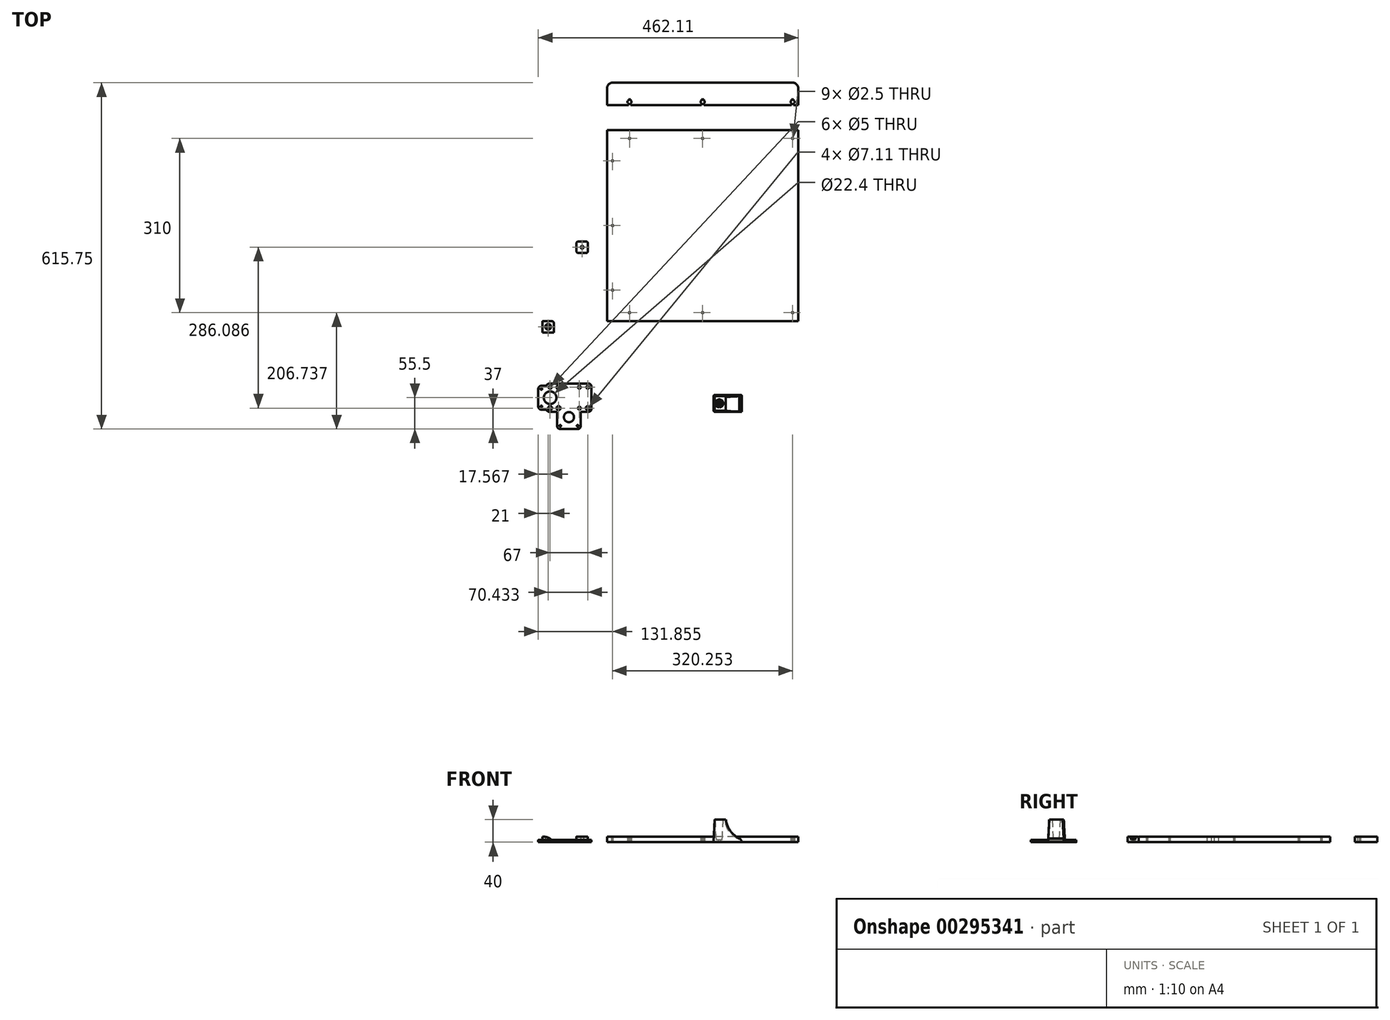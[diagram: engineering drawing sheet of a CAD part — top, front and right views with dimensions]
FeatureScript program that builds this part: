
annotation { "Feature Type Name" : "Feature", "Feature Type Description" : "" }
export const myFeature = defineFeature(function(context is Context, id is Id, definition is map)
    precondition{}
    {
        {
            var Q0;
            Q0=qCreatedBy(makeId("Top.planeOp"),FACE);
            var sketch = newSketch(context, id + "F0", { "sketchPlane" : qUnion([Q0])});
            skLineSegment(sketch, "E0.left", {"start": v(-18.5, 18.5) * mm, "end": v(-18.5, -18.5) * mm, "construction": true});
            skLineSegment(sketch, "E0.right", {"start": v(18.5, 18.5) * mm, "end": v(18.5, -18.5) * mm, "construction": true});
            skCircle(sketch, "E1", {"center": v(-18.5, 18.5) * mm, "radius": 3.56 * mm});
            skCircle(sketch, "E2", {"center": v(18.5, 18.5) * mm, "radius": 2.5 * mm});
            skCircle(sketch, "E3", {"center": v(18.5, -18.5) * mm, "radius": 2.5 * mm});
            skCircle(sketch, "E4", {"center": v(-18.5, -18.5) * mm, "radius": 3.56 * mm});
            skLineSegment(sketch, "E5.bottom", {"start": v(-35, 25) * mm, "end": v(35, 25) * mm});
            skLineSegment(sketch, "E5.top", {"start": v(-35, -25) * mm, "end": v(0.1, -25) * mm});
            skLineSegment(sketch, "E5.right", {"start": v(40, 20) * mm, "end": v(40, -20) * mm});
            skPoint(sketch, "E6.visualSharp", {"position": v(-40, 25) * mm});
            skArc(sketch, "E6.filletArc", {"start": v(-35, 25) * mm, "mid": v(-38.54, 23.54) * mm, "end": v(-40, 20) * mm});
            skPoint(sketch, "E7.visualSharp", {"position": v(40, 25) * mm});
            skArc(sketch, "E7.filletArc", {"start": v(40, 20) * mm, "mid": v(38.54, 23.54) * mm, "end": v(35, 25) * mm});
            skPoint(sketch, "E8.visualSharp", {"position": v(40, -25) * mm});
            skArc(sketch, "E8.filletArc", {"start": v(35, -25) * mm, "mid": v(38.54, -23.54) * mm, "end": v(40, -20) * mm});
            skPoint(sketch, "E9.visualSharp", {"position": v(-40, -25) * mm});
            skArc(sketch, "E9.filletArc", {"start": v(-40, -20) * mm, "mid": v(-38.54, -23.54) * mm, "end": v(-35, -25) * mm});
            skLineSegment(sketch, "E10.bottom", {"start": v(407.6, 136.24) * mm, "end": v(67.6, 136.24) * mm});
            skLineSegment(sketch, "E10.top", {"start": v(407.6, 476.24) * mm, "end": v(67.6, 476.24) * mm});
            skLineSegment(sketch, "E10.left", {"start": v(407.6, 136.24) * mm, "end": v(407.6, 476.24) * mm});
            skLineSegment(sketch, "E10.right", {"start": v(67.6, 136.24) * mm, "end": v(67.6, 476.24) * mm});
            skCircle(sketch, "E11", {"center": v(-33.5, -18.5) * mm, "radius": 3.56 * mm});
            skCircle(sketch, "E12", {"center": v(33.5, -18.5) * mm, "radius": 3.56 * mm});
            skCircle(sketch, "E13", {"center": v(-33.5, 18.5) * mm, "radius": 2.5 * mm});
            skCircle(sketch, "E14", {"center": v(33.5, 18.5) * mm, "radius": 2.5 * mm});
            skPoint(sketch, "E15.middle.positionSnap0", {"position": v(-40, 0) * mm});
            skPoint(sketch, "E15.centerSnap0", {"position": v(-40, 0) * mm});
            skLineSegment(sketch, "E16.top", {"start": v(-15.5, -50) * mm, "end": v(15.5, -50) * mm, "construction": true});
            skLineSegment(sketch, "E16.left", {"start": v(-15.5, -19) * mm, "end": v(-15.5, -50) * mm, "construction": true});
            skLineSegment(sketch, "E16.right", {"start": v(15.5, -19) * mm, "end": v(15.5, -50) * mm, "construction": true});
            skPoint(sketch, "E16.middle", {"position": v(0, -34.5) * mm});
            skLineSegment(sketch, "E17.bottom", {"start": v(21, -13.5) * mm, "end": v(18.5, -13.5) * mm});
            skLineSegment(sketch, "E17.top", {"start": v(16, -55.5) * mm, "end": v(-16, -55.5) * mm});
            skLineSegment(sketch, "E17.left", {"start": v(21, -25) * mm, "end": v(21, -50.5) * mm});
            skLineSegment(sketch, "E17.right", {"start": v(-21, -15.97) * mm, "end": v(-21, -21.03) * mm});
            skCircle(sketch, "E18", {"center": v(0, -34.5) * mm, "radius": 9 * mm});
            skCircle(sketch, "E19", {"center": v(-15.5, -50) * mm, "radius": 1.5 * mm});
            skCircle(sketch, "E20", {"center": v(15.5, -50) * mm, "radius": 1.5 * mm});
            skPoint(sketch, "E21.visualSharp", {"position": v(-21, -55.5) * mm});
            skArc(sketch, "E21.filletArc", {"start": v(-21, -50.5) * mm, "mid": v(-19.54, -54.04) * mm, "end": v(-16, -55.5) * mm});
            skPoint(sketch, "E22.visualSharp", {"position": v(21, -55.5) * mm});
            skArc(sketch, "E22.filletArc", {"start": v(16, -55.5) * mm, "mid": v(19.54, -54.04) * mm, "end": v(21, -50.5) * mm});
            skLineSegment(sketch, "E23.bottom", {"start": v(-49, 15.5) * mm, "end": v(-47.5, 15.5) * mm, "construction": true});
            skLineSegment(sketch, "E23.top", {"start": v(-49, -15.5) * mm, "end": v(-18, -15.5) * mm, "construction": true});
            skLineSegment(sketch, "E23.left", {"start": v(-49, 15.5) * mm, "end": v(-49, -15.5) * mm, "construction": true});
            skLineSegment(sketch, "E23.right", {"start": v(-18, 15.5) * mm, "end": v(-18, -15.5) * mm, "construction": true});
            skCircle(sketch, "E24", {"center": v(-33.5, 0) * mm, "radius": 11.2 * mm});
            skCircle(sketch, "E25", {"center": v(-49, -15.5) * mm, "radius": 1.5 * mm});
            skCircle(sketch, "E26", {"center": v(-49, 15.5) * mm, "radius": 1.5 * mm});
            skPoint(sketch, "E27.visualSharp", {"position": v(-13.5, -20) * mm});
            skLineSegment(sketch, "E28.trimOffspring", {"start": v(-40, 15.5) * mm, "end": v(-18, 15.5) * mm, "construction": true});
            skLineSegment(sketch, "E29.trimOffspring", {"start": v(-21, -25) * mm, "end": v(-21, -50.5) * mm});
            skLineSegment(sketch, "E30.trimOffspring", {"start": v(15.5, -25) * mm, "end": v(35, -25) * mm});
            skLineSegment(sketch, "E31.bottom", {"start": v(-49.5, 21) * mm, "end": v(-39.9, 21) * mm});
            skLineSegment(sketch, "E31.top", {"start": v(-49.5, -21) * mm, "end": v(-39.9, -21) * mm});
            skLineSegment(sketch, "E31.left", {"start": v(-54.5, 16) * mm, "end": v(-54.5, -16) * mm});
            skLineSegment(sketch, "E31.right", {"start": v(-12.5, 21) * mm, "end": v(-12.5, 18.5) * mm});
            skLineSegment(sketch, "E32.trimOffspring", {"start": v(-12.5, -13.5) * mm, "end": v(-12.5, -21) * mm});
            skPoint(sketch, "E33.visualSharp", {"position": v(-54.5, -21) * mm});
            skArc(sketch, "E33.filletArc", {"start": v(-54.5, -16) * mm, "mid": v(-53.04, -19.54) * mm, "end": v(-49.5, -21) * mm});
            skPoint(sketch, "E34.visualSharp", {"position": v(-54.5, 21) * mm});
            skArc(sketch, "E34.filletArc", {"start": v(-49.5, 21) * mm, "mid": v(-53.04, 19.54) * mm, "end": v(-54.5, 16) * mm});
            skLineSegment(sketch, "E35.right", {"start": v(257.17, 4.9) * mm, "end": v(257.17, -25.1) * mm});
            skCircle(sketch, "E36", {"center": v(267.17, -10.1) * mm, "radius": 5 * mm});
            skCircle(sketch, "E37", {"center": v(267.17, -10.1) * mm, "radius": 2 * mm});
            skLineSegment(sketch, "E38.right", {"start": v(307.17, -25.1) * mm, "end": v(307.17, 4.9) * mm});
            skLineSegment(sketch, "E39.bottom", {"start": v(-46.93, 136.1) * mm, "end": v(-26.93, 136.1) * mm});
            skLineSegment(sketch, "E39.top", {"start": v(-46.93, 116.1) * mm, "end": v(-26.93, 116.1) * mm});
            skLineSegment(sketch, "E39.left", {"start": v(-46.93, 136.1) * mm, "end": v(-46.93, 116.1) * mm});
            skLineSegment(sketch, "E39.right", {"start": v(-26.93, 136.1) * mm, "end": v(-26.93, 116.1) * mm});
            skCircle(sketch, "E40", {"center": v(-36.93, 126.1) * mm, "radius": 2.5 * mm});
            skPoint(sketch, "E40.centerSnap0", {"position": v(-36.93, 136.1) * mm});
            skPoint(sketch, "E40.centerSnap1", {"position": v(-46.93, 126.1) * mm});
            skCircle(sketch, "E41", {"center": v(-36.93, 126.1) * mm, "radius": 5 * mm});
            skLineSegment(sketch, "E42", {"start": v(77.6, 136.24) * mm, "end": v(77.6, 476.24) * mm, "construction": true});
            skPoint(sketch, "E43", {"position": v(77.6, 191.24) * mm});
            skPoint(sketch, "E44", {"position": v(77.6, 306.24) * mm});
            skPoint(sketch, "E45", {"position": v(77.36, 421.24) * mm});
            skLineSegment(sketch, "E46", {"start": v(257.17, -25.1) * mm, "end": v(307.17, -25.1) * mm});
            skLineSegment(sketch, "E47", {"start": v(307.17, 4.9) * mm, "end": v(257.17, 4.9) * mm});
            skLineSegment(sketch, "E48", {"start": v(397.6, 136.24) * mm, "end": v(397.6, 476.24) * mm, "construction": true});
            skPoint(sketch, "E49", {"position": v(397.6, 151.24) * mm});
            skPoint(sketch, "E50", {"position": v(397.6, 461.24) * mm});
            skLineSegment(sketch, "E51.bottom", {"start": v(67.6, 520.25) * mm, "end": v(407.6, 520.25) * mm});
            skLineSegment(sketch, "E51.top", {"start": v(77.6, 560.25) * mm, "end": v(397.6, 560.25) * mm});
            skLineSegment(sketch, "E51.left", {"start": v(67.6, 520.25) * mm, "end": v(67.6, 550.25) * mm});
            skLineSegment(sketch, "E51.right", {"start": v(407.6, 520.25) * mm, "end": v(407.6, 550.25) * mm});
            skLineSegment(sketch, "E52", {"start": v(77.6, 151.24) * mm, "end": v(397.6, 151.24) * mm, "construction": true});
            skLineSegment(sketch, "E53", {"start": v(77.6, 461.24) * mm, "end": v(397.6, 461.24) * mm, "construction": true});
            skPoint(sketch, "E54", {"position": v(237.6, 461.24) * mm});
            skPoint(sketch, "E55", {"position": v(237.6, 151.24) * mm});
            skPoint(sketch, "E56", {"position": v(77.6, 520.25) * mm});
            skPoint(sketch, "E57", {"position": v(237.6, 520.25) * mm});
            skPoint(sketch, "E58", {"position": v(397.6, 520.25) * mm});
            skLineSegment(sketch, "E59.bottom", {"start": v(395.6, 530.25) * mm, "end": v(399.6, 530.25) * mm});
            skLineSegment(sketch, "E59.top", {"start": v(395.6, 510.25) * mm, "end": v(399.6, 510.25) * mm});
            skLineSegment(sketch, "E59.left", {"start": v(395.6, 530.25) * mm, "end": v(395.6, 510.25) * mm});
            skLineSegment(sketch, "E59.right", {"start": v(399.6, 530.25) * mm, "end": v(399.6, 510.25) * mm});
            skLineSegment(sketch, "E60.bottom", {"start": v(235.6, 530.25) * mm, "end": v(239.6, 530.25) * mm});
            skLineSegment(sketch, "E60.top", {"start": v(235.6, 510.25) * mm, "end": v(239.6, 510.25) * mm});
            skLineSegment(sketch, "E60.left", {"start": v(235.6, 530.25) * mm, "end": v(235.6, 510.25) * mm});
            skLineSegment(sketch, "E60.right", {"start": v(239.6, 530.25) * mm, "end": v(239.6, 510.25) * mm});
            skLineSegment(sketch, "E61.bottom", {"start": v(109.6, 530.25) * mm, "end": v(105.6, 530.25) * mm});
            skLineSegment(sketch, "E61.top", {"start": v(109.6, 510.25) * mm, "end": v(105.6, 510.25) * mm});
            skLineSegment(sketch, "E61.left", {"start": v(109.6, 530.25) * mm, "end": v(109.6, 510.25) * mm});
            skLineSegment(sketch, "E61.right", {"start": v(105.6, 530.25) * mm, "end": v(105.6, 510.25) * mm});
            skPoint(sketch, "E61.middle", {"position": v(107.6, 520.25) * mm});
            skLineSegment(sketch, "E62.bottom", {"start": v(394.1, 527.72) * mm, "end": v(401.1, 527.72) * mm});
            skLineSegment(sketch, "E62.top", {"start": v(394.1, 524.42) * mm, "end": v(401.1, 524.42) * mm});
            skLineSegment(sketch, "E62.left", {"start": v(394.1, 527.72) * mm, "end": v(394.1, 524.42) * mm});
            skLineSegment(sketch, "E62.right", {"start": v(401.1, 527.72) * mm, "end": v(401.1, 524.42) * mm});
            skPoint(sketch, "E62.middle", {"position": v(397.6, 526.07) * mm});
            skLineSegment(sketch, "E63.bottom", {"start": v(241.1, 527.72) * mm, "end": v(234.1, 527.72) * mm});
            skLineSegment(sketch, "E63.top", {"start": v(241.1, 524.42) * mm, "end": v(234.1, 524.42) * mm});
            skLineSegment(sketch, "E63.left", {"start": v(241.1, 527.72) * mm, "end": v(241.1, 524.42) * mm});
            skLineSegment(sketch, "E63.right", {"start": v(234.1, 527.72) * mm, "end": v(234.1, 524.42) * mm});
            skPoint(sketch, "E63.middle", {"position": v(237.6, 526.07) * mm});
            skPoint(sketch, "E64.visualSharp", {"position": v(67.6, 560.25) * mm});
            skArc(sketch, "E64.filletArc", {"start": v(77.6, 560.25) * mm, "mid": v(70.54, 557.32) * mm, "end": v(67.6, 550.25) * mm});
            skPoint(sketch, "E65.visualSharp", {"position": v(407.6, 560.25) * mm});
            skArc(sketch, "E65.filletArc", {"start": v(407.6, 550.25) * mm, "mid": v(404.68, 557.32) * mm, "end": v(397.6, 560.25) * mm});
            skLineSegment(sketch, "E66.bottom", {"start": v(16, 277.59) * mm, "end": v(31, 277.59) * mm});
            skLineSegment(sketch, "E66.top", {"start": v(16, 257.59) * mm, "end": v(31, 257.59) * mm});
            skLineSegment(sketch, "E66.left", {"start": v(13.5, 275.09) * mm, "end": v(13.5, 260.09) * mm});
            skLineSegment(sketch, "E66.right", {"start": v(33.5, 275.09) * mm, "end": v(33.5, 260.09) * mm});
            skPoint(sketch, "E66.middle", {"position": v(23.5, 267.59) * mm});
            skPoint(sketch, "E67.visualSharp", {"position": v(33.5, 257.59) * mm});
            skArc(sketch, "E67.filletArc", {"start": v(31, 257.59) * mm, "mid": v(32.77, 258.32) * mm, "end": v(33.5, 260.09) * mm});
            skPoint(sketch, "E68.visualSharp", {"position": v(13.5, 257.59) * mm});
            skArc(sketch, "E68.filletArc", {"start": v(13.5, 260.09) * mm, "mid": v(14.23, 258.32) * mm, "end": v(16, 257.59) * mm});
            skPoint(sketch, "E69.visualSharp", {"position": v(33.5, 277.59) * mm});
            skArc(sketch, "E69.filletArc", {"start": v(33.5, 275.09) * mm, "mid": v(32.77, 276.85) * mm, "end": v(31, 277.59) * mm});
            skCircle(sketch, "E70", {"center": v(23.5, 267.59) * mm, "radius": 2.5 * mm});
            skPoint(sketch, "E71.visualSharp", {"position": v(13.5, 277.59) * mm});
            skArc(sketch, "E71.filletArc", {"start": v(16, 277.59) * mm, "mid": v(14.23, 276.85) * mm, "end": v(13.5, 275.09) * mm});
            skPoint(sketch, "E72", {"position": v(107.6, 461.24) * mm});
            skPoint(sketch, "E73", {"position": v(107.6, 151.24) * mm});
            skLineSegment(sketch, "E74.bottom", {"start": v(111.1, 524.42) * mm, "end": v(104.1, 524.42) * mm});
            skLineSegment(sketch, "E74.top", {"start": v(111.1, 527.72) * mm, "end": v(104.1, 527.72) * mm});
            skLineSegment(sketch, "E74.left", {"start": v(111.1, 524.42) * mm, "end": v(111.1, 527.72) * mm});
            skLineSegment(sketch, "E74.right", {"start": v(104.1, 524.42) * mm, "end": v(104.1, 527.72) * mm});
            skPoint(sketch, "E74.middle", {"position": v(107.6, 526.07) * mm});
            skSolve(sketch);
        }
        {
            var Q0;
            Q0=makeQuery(id+"F0.imprint","IMPRINT",FACE,{"disambiguationData":[TD([[makeQuery(id+"F0.imprint","IMPRINT",EDGE,{"derivedFrom":sQuery(id+"F0.wireOp",EDGE,"E1")}),-1.0]])]});
            var Q1;
            Q1=makeQuery(id+"F0.imprint","IMPRINT",FACE,{"disambiguationData":[TD([[makeQuery(id+"F0.imprint","IMPRINT",EDGE,{"derivedFrom":sQuery(id+"F0.wireOp",EDGE,"5QKgwCEY-hStk-wvY1-uHoH-thM2InlFBlLN.top")}),-1.0]])]});
            var Q2;
            Q2=makeQuery(id+"F0.imprint","IMPRINT",FACE,{"disambiguationData":[TD([[makeQuery(id+"F0.imprint","IMPRINT",EDGE,{"derivedFrom":sQuery(id+"F0.wireOp",EDGE,"DSqGHO2r-ZKHx-pAYN-DuYB-4O4wjz5FZ1oX.bottom")}),-1.0]])]});
            var Q3;
            Q3=makeQuery(id+"F0.imprint","IMPRINT",FACE,{"disambiguationData":[TD([[makeQuery(id+"F0.imprint","IMPRINT",EDGE,{"derivedFrom":sQuery(id+"F0.wireOp",EDGE,"HSy17Wos-LkgW-PUzs-iLZR-7mMcprWT0IVK.bottom")}),1.0]])]});
            var Q4;
            Q4=makeQuery(id+"F0.imprint","IMPRINT",FACE,{"disambiguationData":[TD([[makeQuery(id+"F0.imprint","IMPRINT",EDGE,{"derivedFrom":sQuery(id+"F0.wireOp",EDGE,"0c0f4aba-d832-4a81-b14c-29bbfecc0367.right")}),1.0]])]});
            extrude(context, id + "F1", {"entities" : qUnion([Q0, Q1, Q2, Q3, Q4]), "depth" : 4 * mm});
        }
        {
            var Q0;
            Q0=makeQuery(id+"F0.imprint","IMPRINT",FACE,{"disambiguationData":[TD([[makeQuery(id+"F0.imprint","IMPRINT",EDGE,{"derivedFrom":sQuery(id+"F0.wireOp",EDGE,"E10.bottom")}),-1.0]])]});
            var Q1;
            Q1=makeQuery(id+"F0.imprint","IMPRINT",FACE,{"disambiguationData":[TD([[makeQuery(id+"F0.imprint","IMPRINT",EDGE,{"derivedFrom":sQuery(id+"F0.wireOp",EDGE,"E66.bottom")}),-1.0]])]});
            extrude(context, id + "F2", {"entities" : qUnion([Q0, Q1]), "depth" : 10 * mm});
        }
        {
            var Q0;
            Q0=makeQuery(id+"F0.imprint","IMPRINT",FACE,{"disambiguationData":[TD([[makeQuery(id+"F0.imprint","IMPRINT",EDGE,{"derivedFrom":sQuery(id+"F0.wireOp",EDGE,"E35.bottom")}),1.0]])]});
            var Q1;
            Q1=makeQuery(id+"F0.imprint","IMPRINT",FACE,{"disambiguationData":[TD([[makeQuery(id+"F0.imprint","IMPRINT",EDGE,{"derivedFrom":sQuery(id+"F0.wireOp",EDGE,"E35.right")}),1.0]])]});
            extrude(context, id + "F3", {"entities" : qUnion([Q0, Q1]), "depth" : 40 * mm, "hasDraft" : true, "draftAngle" : 3 * degree, "draftPullDirection" : true});
        }
        {
            var Q0;
            Q0=makeQuery(id+"F0.imprint","IMPRINT",FACE,{"disambiguationData":[TD([[makeQuery(id+"F0.imprint","IMPRINT",EDGE,{"derivedFrom":sQuery(id+"F0.wireOp",EDGE,"E36")}),1.0]])]});
            extrude(context, id + "F4", {"entities" : qUnion([Q0]), "operationType" : NewBodyOperationType.ADD, "depth" : 4 * mm, "hasDraft" : true, "draftAngle" : 3 * degree});
        }
        {
            var Q0;
            Q0=qCreatedBy(makeId("Front.planeOp"),FACE);
            var sketch = newSketch(context, id + "F5", { "sketchPlane" : qUnion([Q0])});
            skArc(sketch, "E75", {"start": v(307.17, 0) * mm, "mid": v(305.91, 3.8) * mm, "end": v(302.9, 6.41) * mm});
            skArc(sketch, "E76", {"start": v(278.53, 41.5) * mm, "mid": v(286.23, 20.84) * mm, "end": v(302.9, 6.41) * mm});
            skLineSegment(sketch, "E77", {"start": v(278.53, 41.5) * mm, "end": v(307.17, 41.5) * mm});
            skLineSegment(sketch, "E78", {"start": v(307.17, 41.5) * mm, "end": v(307.17, 0) * mm});
            skSolve(sketch);
        }
        {
            var Q0;
            {var subQ0=sQuery(id+"F5.wireOp",EDGE,"E75");Q0=makeQuery(id+"F5.imprint","IMPRINT",FACE,{"disambiguationData":[TD([[makeQuery(id+"F5.imprint","IMPRINT",EDGE,{"derivedFrom":subQ0}),-1.0]])]});}
            var Q1;
            {var subQ0=sQuery(id+"F5.wireOp",EDGE,"E77");Q1=makeQuery(id+"F5.imprint","IMPRINT",FACE,{"disambiguationData":[TD([[makeQuery(id+"F5.imprint","IMPRINT",EDGE,{"derivedFrom":subQ0}),-1.0]])]});}
            extrude(context, id + "F6", {"entities" : qUnion([Q0, Q1]), "operationType" : NewBodyOperationType.REMOVE, "depth" : 39.1 * mm, "hasSecondDirection" : true, "secondDirectionOppositeDirection" : true, "secondDirectionDepth" : 25 * mm});
        }
        {
            var Q0;
            Q0=makeQuery(id+"F3.opExtrude","SWEPT_EDGE",EDGE,{"disambiguationData":[OSD([sQuery(id+"F0.wireOp",EDGE,"E35.right"),sQuery(id+"F0.wireOp",EDGE,"E47")])]});
            var Q1;
            Q1=makeQuery(id+"F3.opExtrude","SWEPT_EDGE",EDGE,{"disambiguationData":[OSD([sQuery(id+"F0.wireOp",EDGE,"E35.right"),sQuery(id+"F0.wireOp",EDGE,"E46")])]});
            var Q2;
            Q2=makeQuery(id+"F3.opExtrude","SWEPT_EDGE",EDGE,{"disambiguationData":[OSD([sQuery(id+"F0.wireOp",EDGE,"E35.right"),sQuery(id+"F0.wireOp",EDGE,"E47")])]});
            var Q3;
            Q3=makeQuery(id+"F6.boolean.opBoolean","COPY",EDGE,{"derivedFrom":makeQuery(id+"F6.opExtrude","CAP_EDGE",EDGE,{"disambiguationData":[OSD([sQuery(id+"F5.wireOp",EDGE,"E75")])],"isStart":true})});
            var Q4;
            {var subQ0=sQuery(id+"F0.wireOp",EDGE,"E36");Q4=makeQuery(id+"F6.boolean.opBoolean","INTERSECT",EDGE,{"derivedFrom":[makeQuery(id+"F4.boolean.opBoolean","MERGE",FACE,{"derivedFrom":[makeQuery(id+"F3.opExtrude","CAP_FACE",FACE,{"disambiguationData":[OSD([sQuery(id+"F0.wireOp",EDGE,"E35.right"),subQ0,sQuery(id+"F0.wireOp",EDGE,"E38.right"),sQuery(id+"F0.wireOp",EDGE,"E46"),sQuery(id+"F0.wireOp",EDGE,"E47")])],"isStart":true}),makeQuery(id+"F4.opExtrude","CAP_FACE",FACE,{"disambiguationData":[OSD([subQ0,sQuery(id+"F0.wireOp",EDGE,"E37")])],"isStart":true})]}),makeQuery(id+"F6.opExtrude","SWEPT_FACE",FACE,{"disambiguationData":[OSD([sQuery(id+"F5.wireOp",EDGE,"E75")])]})]});}
            var Q5;
            Q5=makeQuery(id+"F6.boolean.opBoolean","INTERSECT",EDGE,{"derivedFrom":[makeQuery(id+"F3.opExtrude","SWEPT_FACE",FACE,{"disambiguationData":[OSD([sQuery(id+"F0.wireOp",EDGE,"E47")])]}),makeQuery(id+"F6.opExtrude","SWEPT_FACE",FACE,{"disambiguationData":[OSD([sQuery(id+"F5.wireOp",EDGE,"E75")])]})]});
            fillet(context, id + "F7", {"entities" : qUnion([Q0, Q1, Q2, Q3, Q4, Q5]), "radius" : 2 * mm, "tangentPropagation" : true, "allowEdgeOverflow" : false});
        }
        {
            var Q0;
            Q0=makeQuery(id+"F0.imprint","IMPRINT",FACE,{"disambiguationData":[TD([[makeQuery(id+"F0.imprint","IMPRINT",EDGE,{"derivedFrom":sQuery(id+"F0.wireOp",EDGE,"E39.bottom")}),-1.0]])]});
            extrude(context, id + "F8", {"entities" : qUnion([Q0]), "depth" : 10 * mm});
        }
        {
            var Q0;
            Q0=makeQuery(id+"F0.imprint","IMPRINT",FACE,{"disambiguationData":[TD([[makeQuery(id+"F0.imprint","IMPRINT",EDGE,{"derivedFrom":sQuery(id+"F0.wireOp",EDGE,"E40")}),-1.0]])]});
            extrude(context, id + "F9", {"entities" : qUnion([Q0]), "operationType" : NewBodyOperationType.ADD, "depth" : 4 * mm});
        }
        {
            var Q0;
            Q0=makeQuery(id+"F8.opExtrude","SWEPT_FACE",FACE,{"disambiguationData":[OSD([sQuery(id+"F0.wireOp",EDGE,"E39.top")])]});
            var sketch = newSketch(context, id + "F10", { "sketchPlane" : qUnion([Q0])});
            skArc(sketch, "E79", {"start": v(-26.93, 0) * mm, "mid": v(-35.75, 7.36) * mm, "end": v(-46.93, 10) * mm});
            skSolve(sketch);
        }
        {
            var Q0;
            Q0=makeQuery(id+"F10.imprint","IMPRINT",FACE,{"disambiguationData":[TD([[makeQuery(id+"F10.imprint","IMPRINT",EDGE,{"derivedFrom":sQuery(id+"F10.wireOp",EDGE,"E79")}),-1.0]])]});
            extrude(context, id + "F11", {"entities" : qUnion([Q0]), "operationType" : NewBodyOperationType.REMOVE, "oppositeDirection" : true, "depth" : 25 * mm});
        }
        {
            var Q0;
            Q0=makeQuery(id+"F11.boolean.opBoolean","COPY",EDGE,{"derivedFrom":makeQuery(id+"F11.opExtrude","CAP_EDGE",EDGE,{"disambiguationData":[OSD([sQuery(id+"F10.wireOp",EDGE,"E79")])],"isStart":true})});
            var Q1;
            Q1=makeQuery(id+"F11.boolean.opBoolean","INTERSECT",EDGE,{"derivedFrom":[makeQuery(id+"F8.opExtrude","SWEPT_FACE",FACE,{"disambiguationData":[OSD([sQuery(id+"F0.wireOp",EDGE,"E39.bottom")])]}),makeQuery(id+"F11.opExtrude","SWEPT_FACE",FACE,{"disambiguationData":[OSD([sQuery(id+"F10.wireOp",EDGE,"E79")])]})]});
            fillet(context, id + "F12", {"entities" : qUnion([Q0, Q1]), "radius" : 3 * mm, "tangentPropagation" : true, "allowEdgeOverflow" : false});
        }
        {
            var Q0;
            Q0=sQuery(id+"F0.wireOp",VERTEX,"dd571d82-195f-4a9d-bc1b-d0bfa332f0c7");
            var Q1;
            Q1=sQuery(id+"F0.wireOp",VERTEX,"E43");
            var Q2;
            Q2=sQuery(id+"F0.wireOp",VERTEX,"E44");
            var Q3;
            Q3=sQuery(id+"F0.wireOp",VERTEX,"E45");
            var Q4;
            Q4=sQuery(id+"F0.wireOp",VERTEX,"4b80c046-3122-48b7-a17c-33549950ae94");
            var Q5;
            Q5=sQuery(id+"F0.wireOp",VERTEX,"E49");
            var Q6;
            Q6=sQuery(id+"F0.wireOp",VERTEX,"E50");
            var Q7;
            Q7=sQuery(id+"F0.wireOp",VERTEX,"E54");
            var Q8;
            Q8=sQuery(id+"F0.wireOp",VERTEX,"E55");
            var Q9;
            Q9=sQuery(id+"F0.wireOp",VERTEX,"E72");
            var Q10;
            Q10=sQuery(id+"F0.wireOp",VERTEX,"E73");
            var Q11;
            Q11=makeQuery(id+"F2.opExtrude","SWEPT_BODY",BODY,{"disambiguationData":[OSD([sQuery(id+"F0.wireOp",EDGE,"E10.bottom"),sQuery(id+"F0.wireOp",EDGE,"E10.top"),sQuery(id+"F0.wireOp",EDGE,"E10.left"),sQuery(id+"F0.wireOp",EDGE,"E10.right")])]});
            hole(context, id + "F13", {"style" : HoleStyle.SIMPLE, "endStyle" : HoleEndStyle.BLIND, "oppositeDirection" : true, "holeDiameter" : 2.5 * mm, "holeDepth" : 20 * mm, "tappedDepth" : 12 * mm, "tapClearance" : 3, "locations" : qUnion([Q0, Q1, Q2, Q3, Q4, Q5, Q6, Q7, Q8, Q9, Q10]), "scope" : qUnion([Q11]), "startStyle" : HoleStartStyle.PART});
        }
        {
            var Q0;
            Q0=makeQuery(id+"F0.imprint","IMPRINT",FACE,{"disambiguationData":[TD([[makeQuery(id+"F0.imprint","IMPRINT",EDGE,{"derivedFrom":sQuery(id+"F0.wireOp",EDGE,"E51.bottom")}),1.0]])]});
            extrude(context, id + "F14", {"entities" : qUnion([Q0]), "depth" : 10 * mm});
        }
    });
